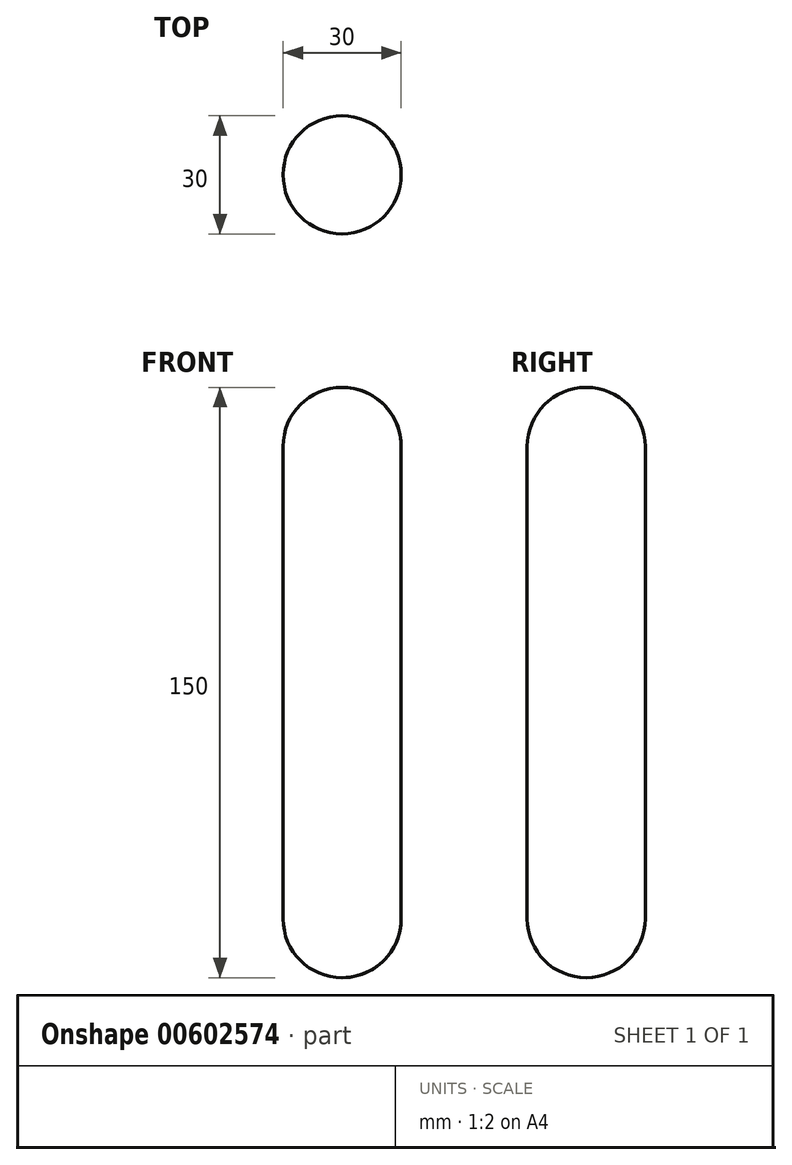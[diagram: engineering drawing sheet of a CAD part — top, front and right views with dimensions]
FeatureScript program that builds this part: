
annotation { "Feature Type Name" : "Feature", "Feature Type Description" : "" }
export const myFeature = defineFeature(function(context is Context, id is Id, definition is map)
    precondition{}
    {
        {
            var Q0;
            Q0=qCreatedBy(makeId("Top.planeOp"),FACE);
            var sketch = newSketch(context, id + "F0", { "sketchPlane" : qUnion([Q0])});
            skCircle(sketch, "E0", {"center": v(0, 0) * mm, "radius": 15 * mm});
            skSolve(sketch);
        }
        {
            var Q0;
            Q0=makeQuery(id+"F0.imprint","IMPRINT",FACE,{"disambiguationData":[TD([[makeQuery(id+"F0.imprint","IMPRINT",EDGE,{"derivedFrom":sQuery(id+"F0.wireOp",EDGE,"E0")}),1.0]])]});
            extrude(context, id + "F1", {"entities" : qUnion([Q0]), "endBound" : BoundingType.SYMMETRIC, "depth" : 150 * mm, "offsetDistance" : 25 * mm});
        }
        {
            var Q0;
            Q0=makeQuery(id+"F1.opExtrude","CAP_FACE",FACE,{"disambiguationData":[OSD([sQuery(id+"F0.wireOp",EDGE,"E0")])],"isStart":false});
            var Q1;
            Q1=makeQuery(id+"F1.opExtrude","CAP_FACE",FACE,{"disambiguationData":[OSD([sQuery(id+"F0.wireOp",EDGE,"E0")])],"isStart":true});
            fillet(context, id + "F2", {"entities" : qUnion([Q0, Q1]), "radius" : 15 * mm, "tangentPropagation" : true, "allowEdgeOverflow" : false});
        }
    });
